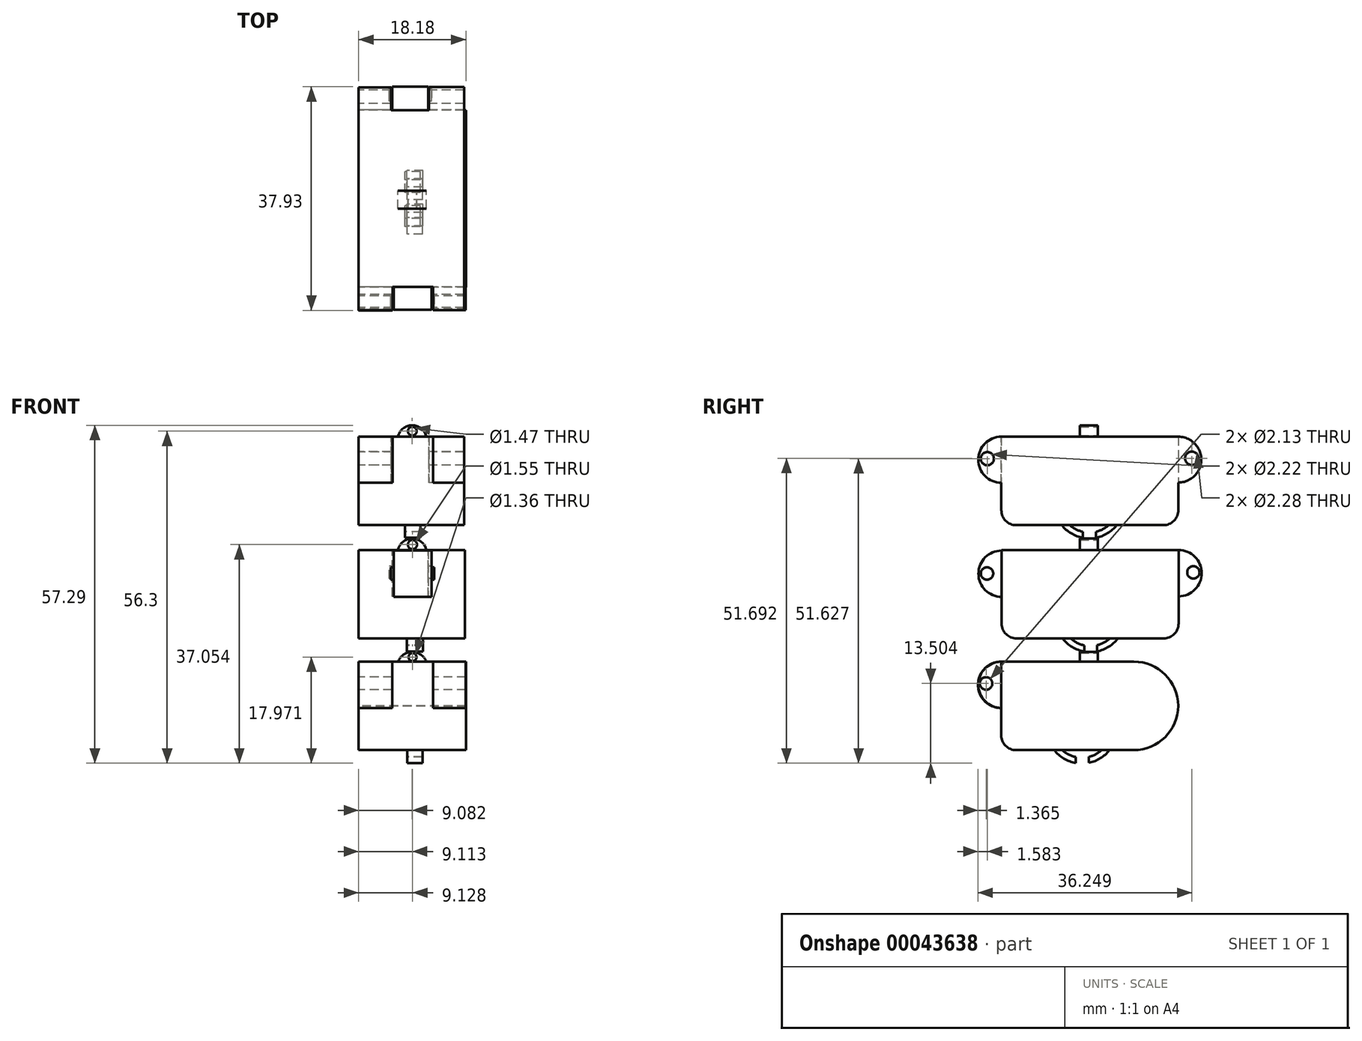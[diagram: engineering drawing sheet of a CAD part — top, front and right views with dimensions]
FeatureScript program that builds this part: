
annotation { "Feature Type Name" : "Feature", "Feature Type Description" : "" }
export const myFeature = defineFeature(function(context is Context, id is Id, definition is map)
    precondition{}
    {
        {
            var Q0;
            Q0=qCreatedBy(makeId("Right.planeOp"),FACE);
            var sketch = newSketch(context, id + "F0", { "sketchPlane" : qUnion([Q0])});
            skLineSegment(sketch, "E0.bottom", {"start": v(-13.77, 7.12) * mm, "end": v(11.16, 7.12) * mm});
            skLineSegment(sketch, "E0.top", {"start": v(-13.77, -7.88) * mm, "end": v(11.16, -7.88) * mm});
            skLineSegment(sketch, "E0.left", {"start": v(-16.3, 4.58) * mm, "end": v(-16.3, -5.34) * mm});
            skLineSegment(sketch, "E0.right", {"start": v(13.7, 4.58) * mm, "end": v(13.7, -5.34) * mm});
            skPoint(sketch, "E1.visualSharp", {"position": v(-16.3, -7.88) * mm});
            skArc(sketch, "E1.filletArc", {"start": v(-16.3, -5.34) * mm, "mid": v(-15.56, -7.14) * mm, "end": v(-13.77, -7.88) * mm});
            skPoint(sketch, "E2.visualSharp", {"position": v(13.7, -7.88) * mm});
            skArc(sketch, "E2.filletArc", {"start": v(11.16, -7.88) * mm, "mid": v(12.96, -7.14) * mm, "end": v(13.7, -5.34) * mm});
            skLineSegment(sketch, "E3", {"start": v(-13.77, 7.12) * mm, "end": v(-16.3, 7.12) * mm});
            skLineSegment(sketch, "E4", {"start": v(-16.3, 4.58) * mm, "end": v(-16.3, 7.12) * mm});
            skPoint(sketch, "E5", {"position": v(-16.3, 7.12) * mm});
            skLineSegment(sketch, "E6", {"start": v(13.7, 4.58) * mm, "end": v(13.7, 7.12) * mm});
            skLineSegment(sketch, "E7", {"start": v(13.7, 7.12) * mm, "end": v(11.16, 7.12) * mm});
            skSolve(sketch);
        }
        {
            var Q0;
            Q0 = qSketchRegion(id + "F0", true);
            extrude(context, id + "F1", {"entities" : qUnion([Q0]), "depth" : 18 * mm});
        }
        {
            var Q0;
            Q0=qCreatedBy(makeId("Right.planeOp"),FACE);
            var sketch = newSketch(context, id + "F2", { "sketchPlane" : qUnion([Q0])});
            skArc(sketch, "E8", {"start": v(-16.3, 7.03) * mm, "mid": v(-20.23, 3.1) * mm, "end": v(-16.3, -0.81) * mm});
            skLineSegment(sketch, "E9", {"start": v(-16.3, 7.03) * mm, "end": v(-16.3, -0.81) * mm});
            skLineSegment(sketch, "E10", {"start": v(-16.3, 3.1) * mm, "end": v(-20.23, 3.1) * mm});
            skSolve(sketch);
        }
        {
            var Q0;
            Q0=makeQuery(id+"F2.imprint","IMPRINT",FACE,{"disambiguationData":[TD([[makeQuery(id+"F2.imprint","IMPRINT",EDGE,{"derivedFrom":sQuery(id+"F2.wireOp",EDGE,"E8")}),1.0]])]});
            extrude(context, id + "F3", {"entities" : qUnion([Q0]), "operationType" : NewBodyOperationType.ADD, "depth" : 12.37 * mm, "hasSecondDirection" : true, "secondDirectionOppositeDirection" : false, "secondDirectionDepth" : 5.95 * mm});
        }
        {
            var Q0;
            Q0=qCreatedBy(makeId("Right.planeOp"),FACE);
            var sketch = newSketch(context, id + "F4", { "sketchPlane" : qUnion([Q0])});
            skLineSegment(sketch, "E11.bottom", {"start": v(-13.8, 11.34) * mm, "end": v(11.11, 11.34) * mm});
            skLineSegment(sketch, "E11.top", {"start": v(-13.8, 26.35) * mm, "end": v(11.11, 26.35) * mm});
            skLineSegment(sketch, "E11.left", {"start": v(-16.35, 13.88) * mm, "end": v(-16.35, 23.81) * mm});
            skLineSegment(sketch, "E11.right", {"start": v(13.65, 13.88) * mm, "end": v(13.65, 23.81) * mm});
            skPoint(sketch, "E12.visualSharp", {"position": v(-16.35, 26.35) * mm});
            skPoint(sketch, "E13.visualSharp", {"position": v(-16.35, 11.34) * mm});
            skArc(sketch, "E13.filletArc", {"start": v(-16.35, 13.88) * mm, "mid": v(-15.6, 12.09) * mm, "end": v(-13.8, 11.34) * mm});
            skPoint(sketch, "E14.visualSharp", {"position": v(13.65, 26.35) * mm});
            skPoint(sketch, "E15.visualSharp", {"position": v(13.65, 11.34) * mm});
            skArc(sketch, "E15.filletArc", {"start": v(11.11, 11.34) * mm, "mid": v(12.9, 12.09) * mm, "end": v(13.65, 13.88) * mm});
            skLineSegment(sketch, "E16", {"start": v(-16.35, 23.81) * mm, "end": v(-16.35, 26.35) * mm});
            skLineSegment(sketch, "E17", {"start": v(-13.8, 26.35) * mm, "end": v(-16.35, 26.35) * mm});
            skLineSegment(sketch, "E18", {"start": v(11.11, 26.35) * mm, "end": v(13.65, 26.35) * mm});
            skLineSegment(sketch, "E19", {"start": v(13.65, 23.81) * mm, "end": v(13.65, 26.35) * mm});
            skSolve(sketch);
        }
        {
            var Q0;
            Q0 = qSketchRegion(id + "F4", true);
            extrude(context, id + "F5", {"entities" : qUnion([Q0]), "depth" : 17.88 * mm});
        }
        {
            var Q0;
            Q0=qCreatedBy(makeId("Right.planeOp"),FACE);
            var sketch = newSketch(context, id + "F6", { "sketchPlane" : qUnion([Q0])});
            skLineSegment(sketch, "E20", {"start": v(13.65, 26.35) * mm, "end": v(13.65, 18.58) * mm});
            skArc(sketch, "E21", {"start": v(13.65, 18.58) * mm, "mid": v(17.54, 22.47) * mm, "end": v(13.65, 26.35) * mm});
            skSolve(sketch);
        }
        {
            var Q0;
            Q0=makeQuery(id+"F6.imprint","IMPRINT",FACE,{"disambiguationData":[TD([[makeQuery(id+"F6.imprint","IMPRINT",EDGE,{"derivedFrom":sQuery(id+"F6.wireOp",EDGE,"E20")}),1.0]])]});
            extrude(context, id + "F7", {"entities" : qUnion([Q0]), "operationType" : NewBodyOperationType.ADD, "depth" : 5.5 * mm});
        }
        {
            var Q0;
            Q0=qCreatedBy(makeId("Right.planeOp"),FACE);
            var sketch = newSketch(context, id + "F8", { "sketchPlane" : qUnion([Q0])});
            skArc(sketch, "E22", {"start": v(13.65, 18.57) * mm, "mid": v(17.56, 22.46) * mm, "end": v(13.65, 26.35) * mm});
            skLineSegment(sketch, "E23", {"start": v(13.65, 26.35) * mm, "end": v(13.65, 18.57) * mm});
            skSolve(sketch);
        }
        {
            var Q0;
            Q0 = qSketchRegion(id + "F8", true);
            extrude(context, id + "F9", {"entities" : qUnion([Q0]), "operationType" : NewBodyOperationType.ADD, "depth" : 17.88 * mm, "hasSecondDirection" : true, "secondDirectionOppositeDirection" : false, "secondDirectionDepth" : 11.92 * mm});
        }
        {
            var Q0;
            Q0=qCreatedBy(makeId("Right.planeOp"),FACE);
            var sketch = newSketch(context, id + "F10", { "sketchPlane" : qUnion([Q0])});
            skArc(sketch, "E24", {"start": v(-16.35, 26.35) * mm, "mid": v(-20.25, 22.43) * mm, "end": v(-16.33, 18.53) * mm});
            skLineSegment(sketch, "E25", {"start": v(-16.35, 26.35) * mm, "end": v(-16.33, 18.53) * mm});
            skSolve(sketch);
        }
        {
            var Q0;
            Q0 = qSketchRegion(id + "F10", true);
            extrude(context, id + "F11", {"entities" : qUnion([Q0]), "operationType" : NewBodyOperationType.ADD, "depth" : 5.75 * mm});
        }
        {
            var Q0;
            Q0=qCreatedBy(makeId("Right.planeOp"),FACE);
            var sketch = newSketch(context, id + "F12", { "sketchPlane" : qUnion([Q0])});
            skArc(sketch, "E26", {"start": v(-16.35, 26.35) * mm, "mid": v(-20.24, 22.44) * mm, "end": v(-16.35, 18.53) * mm});
            skLineSegment(sketch, "E27", {"start": v(-16.35, 26.35) * mm, "end": v(-16.35, 18.53) * mm});
            skSolve(sketch);
        }
        {
            var Q0;
            Q0 = qSketchRegion(id + "F12", true);
            extrude(context, id + "F13", {"entities" : qUnion([Q0]), "operationType" : NewBodyOperationType.ADD, "depth" : 17.88 * mm, "hasSecondDirection" : true, "secondDirectionOppositeDirection" : false, "secondDirectionDepth" : 12.64 * mm});
        }
        {
            var Q0;
            Q0=qCreatedBy(makeId("Right.planeOp"),FACE);
            var sketch = newSketch(context, id + "F14", { "sketchPlane" : qUnion([Q0])});
            skCircle(sketch, "E28", {"center": v(-18.72, 22.62) * mm, "radius": 1.11 * mm});
            skCircle(sketch, "E29", {"center": v(15.95, 22.68) * mm, "radius": 1.14 * mm});
            skSolve(sketch);
        }
        {
            var Q0;
            Q0 = qSketchRegion(id + "F14", true);
            extrude(context, id + "F15", {"entities" : qUnion([Q0]), "operationType" : NewBodyOperationType.REMOVE, "depth" : 25.4 * mm, "hasSecondDirection" : true, "secondDirectionOppositeDirection" : true, "secondDirectionDepth" : 25.4 * mm});
        }
        {
            var Q0;
            Q0=qCreatedBy(makeId("Right.planeOp"),FACE);
            var sketch = newSketch(context, id + "F16", { "sketchPlane" : qUnion([Q0])});
            skLineSegment(sketch, "E30.bottom", {"start": v(-13.82, -11.81) * mm, "end": v(6.11, -11.81) * mm});
            skLineSegment(sketch, "E30.top", {"start": v(-13.82, -26.82) * mm, "end": v(6.11, -26.82) * mm});
            skLineSegment(sketch, "E30.left", {"start": v(-16.36, -14.35) * mm, "end": v(-16.36, -24.28) * mm});
            skLineSegment(sketch, "E30.right", {"start": v(13.63, -19.3) * mm, "end": v(13.63, -19.33) * mm});
            skPoint(sketch, "E31.visualSharp", {"position": v(13.63, -11.81) * mm});
            skArc(sketch, "E31.filletArc", {"start": v(13.63, -19.33) * mm, "mid": v(11.43, -14.02) * mm, "end": v(6.11, -11.81) * mm});
            skPoint(sketch, "E32.visualSharp", {"position": v(13.63, -26.82) * mm});
            skArc(sketch, "E32.filletArc", {"start": v(6.11, -26.82) * mm, "mid": v(11.43, -24.62) * mm, "end": v(13.63, -19.3) * mm});
            skPoint(sketch, "E33.visualSharp", {"position": v(-16.36, -11.81) * mm});
            skPoint(sketch, "E34.visualSharp", {"position": v(-16.36, -26.82) * mm});
            skArc(sketch, "E34.filletArc", {"start": v(-16.36, -24.28) * mm, "mid": v(-15.62, -26.08) * mm, "end": v(-13.82, -26.82) * mm});
            skLineSegment(sketch, "E35", {"start": v(-16.36, -11.81) * mm, "end": v(-16.36, -14.35) * mm});
            skLineSegment(sketch, "E36", {"start": v(-16.36, -11.81) * mm, "end": v(-13.82, -11.81) * mm});
            skSolve(sketch);
        }
        {
            var Q0;
            Q0 = qSketchRegion(id + "F16", true);
            extrude(context, id + "F17", {"entities" : qUnion([Q0]), "depth" : 18.18 * mm});
        }
        {
            var Q0;
            Q0=qCreatedBy(makeId("Right.planeOp"),FACE);
            var sketch = newSketch(context, id + "F18", { "sketchPlane" : qUnion([Q0])});
            skLineSegment(sketch, "E37", {"start": v(-16.36, -11.82) * mm, "end": v(-16.36, -19.66) * mm});
            skArc(sketch, "E38", {"start": v(-16.36, -11.82) * mm, "mid": v(-20.3, -15.74) * mm, "end": v(-16.36, -19.66) * mm});
            skSolve(sketch);
        }
        {
            var Q0;
            Q0 = qSketchRegion(id + "F18", true);
            extrude(context, id + "F19", {"entities" : qUnion([Q0]), "operationType" : NewBodyOperationType.ADD, "depth" : 5.68 * mm});
        }
        {
            var Q0;
            Q0=qCreatedBy(makeId("Right.planeOp"),FACE);
            var sketch = newSketch(context, id + "F20", { "sketchPlane" : qUnion([Q0])});
            skLineSegment(sketch, "E39", {"start": v(-16.36, -11.81) * mm, "end": v(-16.36, -19.65) * mm});
            skArc(sketch, "E40", {"start": v(-16.36, -11.81) * mm, "mid": v(-20.25, -15.73) * mm, "end": v(-16.36, -19.65) * mm});
            skSolve(sketch);
        }
        {
            var Q0;
            Q0 = qSketchRegion(id + "F20", true);
            extrude(context, id + "F21", {"entities" : qUnion([Q0]), "operationType" : NewBodyOperationType.ADD, "depth" : 18.16 * mm, "hasSecondDirection" : true, "secondDirectionOppositeDirection" : false, "secondDirectionDepth" : 12.64 * mm});
        }
        {
            var Q0;
            Q0=qCreatedBy(makeId("Right.planeOp"),FACE);
            var sketch = newSketch(context, id + "F22", { "sketchPlane" : qUnion([Q0])});
            skCircle(sketch, "E41", {"center": v(-18.78, 3.15) * mm, "radius": 1.05 * mm});
            skSolve(sketch);
        }
        {
            var Q0;
            Q0 = qSketchRegion(id + "F22", true);
            extrude(context, id + "F23", {"entities" : qUnion([Q0]), "operationType" : NewBodyOperationType.ADD, "depth" : 12.8 * mm, "hasSecondDirection" : true, "secondDirectionOppositeDirection" : false, "secondDirectionDepth" : 5.43 * mm});
        }
        {
            var Q0;
            Q0=qCreatedBy(makeId("Right.planeOp"),FACE);
            var sketch = newSketch(context, id + "F24", { "sketchPlane" : qUnion([Q0])});
            skLineSegment(sketch, "E42", {"start": v(13.7, 7.12) * mm, "end": v(13.7, -0.73) * mm});
            skArc(sketch, "E43", {"start": v(13.7, -0.73) * mm, "mid": v(17.63, 3.2) * mm, "end": v(13.7, 7.12) * mm});
            skSolve(sketch);
        }
        {
            var Q0;
            Q0 = qSketchRegion(id + "F24", true);
            extrude(context, id + "F25", {"entities" : qUnion([Q0]), "operationType" : NewBodyOperationType.ADD, "depth" : 11.77 * mm, "hasSecondDirection" : true, "secondDirectionOppositeDirection" : false, "secondDirectionDepth" : 5.67 * mm});
        }
        {
            var Q0;
            Q0=qCreatedBy(makeId("Right.planeOp"),FACE);
            var sketch = newSketch(context, id + "F26", { "sketchPlane" : qUnion([Q0])});
            skCircle(sketch, "E44", {"center": v(16.2, 3.33) * mm, "radius": 1.05 * mm});
            skSolve(sketch);
        }
        {
            var Q0;
            Q0 = qSketchRegion(id + "F26", true);
            extrude(context, id + "F27", {"entities" : qUnion([Q0]), "operationType" : NewBodyOperationType.ADD, "depth" : 12.37 * mm, "hasSecondDirection" : true, "secondDirectionOppositeDirection" : false, "secondDirectionDepth" : 5.15 * mm});
        }
        {
            var Q0;
            Q0=qCreatedBy(makeId("Right.planeOp"),FACE);
            var sketch = newSketch(context, id + "F28", { "sketchPlane" : qUnion([Q0])});
            skCircle(sketch, "E45", {"center": v(-18.93, -15.5) * mm, "radius": 1.07 * mm});
            skSolve(sketch);
        }
        {
            var Q0;
            Q0 = qSketchRegion(id + "F28", true);
            extrude(context, id + "F29", {"entities" : qUnion([Q0]), "operationType" : NewBodyOperationType.REMOVE, "depth" : 25.4 * mm, "hasSecondDirection" : true, "secondDirectionOppositeDirection" : true, "secondDirectionDepth" : 25.4 * mm});
        }
        {
            var Q0;
            Q0=qCreatedBy(makeId("Right.planeOp"),FACE);
            var sketch = newSketch(context, id + "F30", { "sketchPlane" : qUnion([Q0])});
            skLineSegment(sketch, "E46", {"start": v(11.22, 11.38) * mm, "end": v(-13.8, 11.38) * mm, "construction": true});
            skPoint(sketch, "E47", {"position": v(-1.3, 11.38) * mm});
            skArc(sketch, "E48", {"start": v(-6.11, 11.38) * mm, "mid": v(-1.44, 9.1) * mm, "end": v(3.23, 11.38) * mm});
            skLineSegment(sketch, "E49", {"start": v(-6.11, 11.38) * mm, "end": v(-4.76, 11.38) * mm});
            skLineSegment(sketch, "E50", {"start": v(3.23, 11.38) * mm, "end": v(1.88, 11.38) * mm});
            skArc(sketch, "E51", {"start": v(-4.76, 11.38) * mm, "mid": v(-1.44, 10.09) * mm, "end": v(1.88, 11.38) * mm});
            skSolve(sketch);
        }
        {
            var Q0;
            Q0 = qSketchRegion(id + "F30", true);
            extrude(context, id + "F31", {"entities" : qUnion([Q0]), "operationType" : NewBodyOperationType.ADD, "depth" : 10.46 * mm, "hasSecondDirection" : true, "secondDirectionOppositeDirection" : false, "secondDirectionDepth" : 7.84 * mm});
        }
        {
            var Q0;
            Q0=qCreatedBy(makeId("Right.planeOp"),FACE);
            var sketch = newSketch(context, id + "F32", { "sketchPlane" : qUnion([Q0])});
            skLineSegment(sketch, "E52", {"start": v(11.26, -7.87) * mm, "end": v(-13.76, -7.87) * mm, "construction": true});
            skPoint(sketch, "E53", {"position": v(-1.25, -7.87) * mm});
            skArc(sketch, "E54", {"start": v(-5.96, -7.87) * mm, "mid": v(-1.26, -10.18) * mm, "end": v(3.44, -7.87) * mm});
            skLineSegment(sketch, "E55", {"start": v(-5.96, -7.87) * mm, "end": v(-4.58, -7.87) * mm});
            skLineSegment(sketch, "E56", {"start": v(3.44, -7.87) * mm, "end": v(2.06, -7.87) * mm});
            skArc(sketch, "E57", {"start": v(-4.58, -7.87) * mm, "mid": v(-1.26, -9.16) * mm, "end": v(2.06, -7.87) * mm});
            skSolve(sketch);
        }
        {
            var Q0;
            Q0 = qSketchRegion(id + "F32", true);
            extrude(context, id + "F33", {"entities" : qUnion([Q0]), "operationType" : NewBodyOperationType.ADD, "depth" : 10.9 * mm, "hasSecondDirection" : true, "secondDirectionOppositeDirection" : false, "secondDirectionDepth" : 8.17 * mm});
        }
        {
            var Q0;
            Q0=qCreatedBy(makeId("Right.planeOp"),FACE);
            var sketch = newSketch(context, id + "F34", { "sketchPlane" : qUnion([Q0])});
            skLineSegment(sketch, "E58", {"start": v(10.74, -26.82) * mm, "end": v(-14.29, -26.82) * mm, "construction": true});
            skPoint(sketch, "E59", {"position": v(-1.78, -26.82) * mm});
            skArc(sketch, "E60", {"start": v(-7.37, -26.82) * mm, "mid": v(-2.7, -29.1) * mm, "end": v(1.98, -26.82) * mm});
            skLineSegment(sketch, "E61", {"start": v(-7.37, -26.82) * mm, "end": v(-6.01, -26.82) * mm});
            skLineSegment(sketch, "E62", {"start": v(1.98, -26.82) * mm, "end": v(0.62, -26.82) * mm});
            skArc(sketch, "E63", {"start": v(-6.01, -26.82) * mm, "mid": v(-2.7, -28.1) * mm, "end": v(0.62, -26.82) * mm});
            skSolve(sketch);
        }
        {
            var Q0;
            Q0 = qSketchRegion(id + "F34", true);
            extrude(context, id + "F35", {"entities" : qUnion([Q0]), "operationType" : NewBodyOperationType.ADD, "depth" : 10.84 * mm, "hasSecondDirection" : true, "secondDirectionOppositeDirection" : false, "secondDirectionDepth" : 8.2 * mm});
        }
        {
            var Q0;
            Q0=qCreatedBy(makeId("Right.planeOp"),FACE);
            var sketch = newSketch(context, id + "F36", { "sketchPlane" : qUnion([Q0])});
            skLineSegment(sketch, "E64.bottom", {"start": v(-2.53, 10.66) * mm, "end": v(-0.33, 10.66) * mm});
            skLineSegment(sketch, "E64.top", {"start": v(-2.53, 8.46) * mm, "end": v(-0.33, 8.46) * mm});
            skLineSegment(sketch, "E64.left", {"start": v(-2.53, 10.66) * mm, "end": v(-2.53, 8.46) * mm});
            skLineSegment(sketch, "E64.right", {"start": v(-0.33, 10.66) * mm, "end": v(-0.33, 8.46) * mm});
            skLineSegment(sketch, "E65.bottom", {"start": v(-2.3, -8.53) * mm, "end": v(-0.1, -8.53) * mm});
            skLineSegment(sketch, "E65.top", {"start": v(-2.3, -10.73) * mm, "end": v(-0.1, -10.73) * mm});
            skLineSegment(sketch, "E65.left", {"start": v(-2.3, -8.53) * mm, "end": v(-2.3, -10.73) * mm});
            skLineSegment(sketch, "E65.right", {"start": v(-0.1, -8.53) * mm, "end": v(-0.1, -10.73) * mm});
            skLineSegment(sketch, "E66.bottom", {"start": v(-3.71, -27.56) * mm, "end": v(-1.51, -27.56) * mm});
            skLineSegment(sketch, "E66.top", {"start": v(-3.71, -29.76) * mm, "end": v(-1.51, -29.76) * mm});
            skLineSegment(sketch, "E66.left", {"start": v(-3.71, -27.56) * mm, "end": v(-3.71, -29.76) * mm});
            skLineSegment(sketch, "E66.right", {"start": v(-1.51, -27.56) * mm, "end": v(-1.51, -29.76) * mm});
            skSolve(sketch);
        }
        {
            var Q0;
            Q0 = qSketchRegion(id + "F36", true);
            extrude(context, id + "F37", {"entities" : qUnion([Q0]), "operationType" : NewBodyOperationType.REMOVE, "oppositeDirection" : true, "depth" : 25.4 * mm, "hasSecondDirection" : true, "secondDirectionOppositeDirection" : false, "secondDirectionDepth" : 25.4 * mm});
        }
        {
            var Q0;
            Q0=qCreatedBy(makeId("Front.planeOp"),FACE);
            var sketch = newSketch(context, id + "F38", { "sketchPlane" : qUnion([Q0])});
            skArc(sketch, "E67", {"start": v(11.47, 7.11) * mm, "mid": v(9.06, 9.07) * mm, "end": v(6.65, 7.11) * mm});
            skLineSegment(sketch, "E68", {"start": v(6.65, 7.11) * mm, "end": v(11.47, 7.11) * mm});
            skLineSegment(sketch, "E69", {"start": v(6.65, 30.98) * mm, "end": v(6.65, -30.43) * mm, "construction": true});
            skLineSegment(sketch, "E70", {"start": v(11.47, 30.87) * mm, "end": v(11.47, -30.33) * mm, "construction": true});
            skArc(sketch, "E71", {"start": v(11.47, 26.35) * mm, "mid": v(9.06, 28.28) * mm, "end": v(6.65, 26.34) * mm});
            skLineSegment(sketch, "E72", {"start": v(6.65, 26.34) * mm, "end": v(11.47, 26.35) * mm});
            skArc(sketch, "E73", {"start": v(11.47, -11.8) * mm, "mid": v(9.05, -10.18) * mm, "end": v(6.65, -11.83) * mm});
            skLineSegment(sketch, "E74", {"start": v(6.65, -11.83) * mm, "end": v(11.47, -11.8) * mm});
            skSolve(sketch);
        }
        {
            var Q0;
            Q0 = qSketchRegion(id + "F38", true);
            extrude(context, id + "F39", {"entities" : qUnion([Q0]), "depth" : 3.02 * mm});
        }
        {
            var Q0;
            Q0=qCreatedBy(makeId("Front.planeOp"),FACE);
            var sketch = newSketch(context, id + "F40", { "sketchPlane" : qUnion([Q0])});
            skCircle(sketch, "E75", {"center": v(9.08, 27.3) * mm, "radius": 0.74 * mm});
            skCircle(sketch, "E76", {"center": v(9.11, 8.04) * mm, "radius": 0.77 * mm});
            skCircle(sketch, "E77", {"center": v(9.13, -11.04) * mm, "radius": 0.68 * mm});
            skSolve(sketch);
        }
        {
            var Q0;
            Q0 = qSketchRegion(id + "F40", true);
            extrude(context, id + "F41", {"entities" : qUnion([Q0]), "operationType" : NewBodyOperationType.REMOVE, "depth" : 25.4 * mm, "hasSecondDirection" : true, "secondDirectionOppositeDirection" : true, "secondDirectionDepth" : 25.4 * mm});
        }
    });
